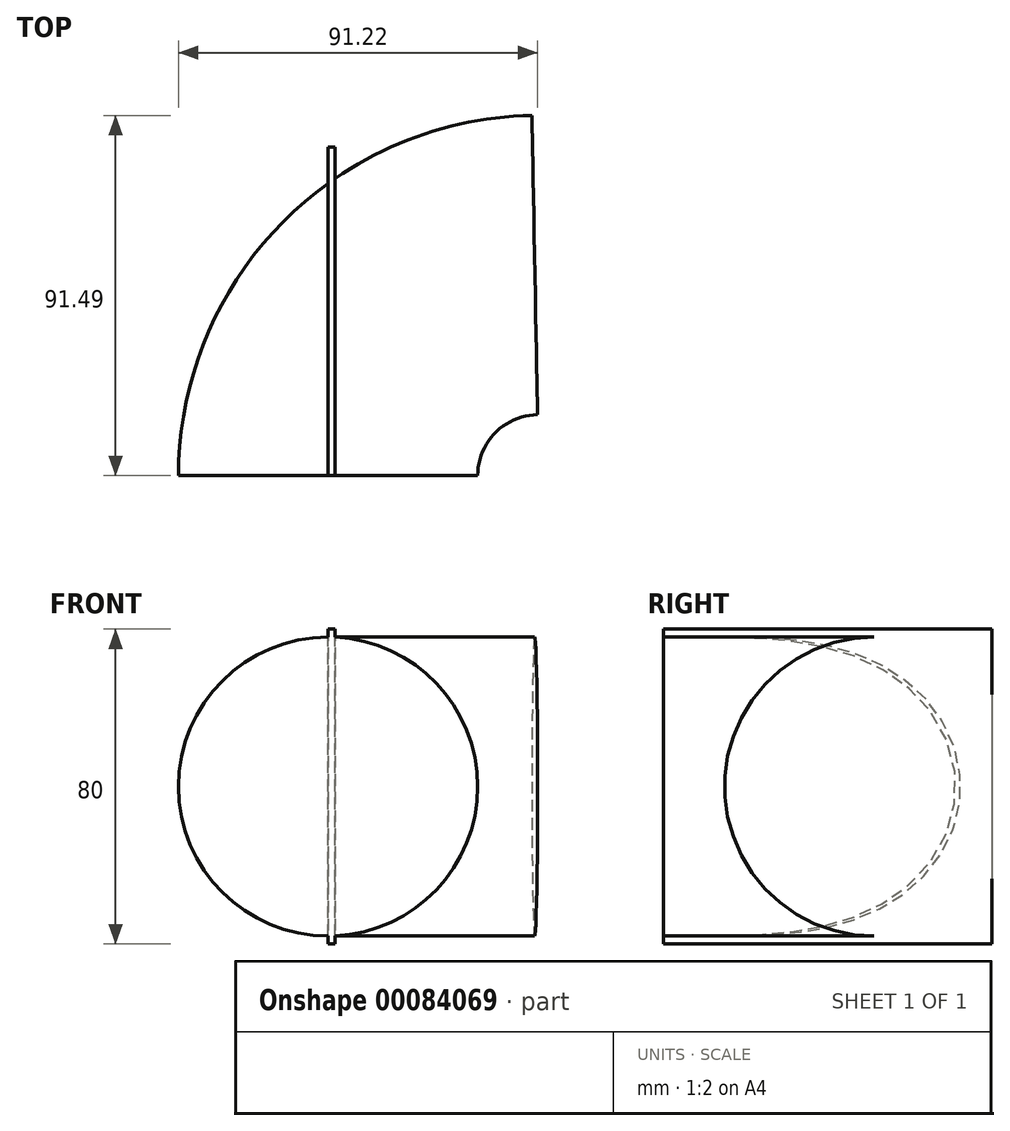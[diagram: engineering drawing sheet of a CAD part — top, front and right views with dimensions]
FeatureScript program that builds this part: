
annotation { "Feature Type Name" : "Feature", "Feature Type Description" : "" }
export const myFeature = defineFeature(function(context is Context, id is Id, definition is map)
    precondition{}
    {
        {
            var Q0;
            Q0=qCreatedBy(makeId("Front.planeOp"),FACE);
            var sketch = newSketch(context, id + "F0", { "sketchPlane" : qUnion([Q0])});
            skCircle(sketch, "E0", {"center": v(0, 0) * mm, "radius": 38 * mm});
            skSolve(sketch);
        }
        {
            var Q0;
            Q0=qCreatedBy(makeId("Top.planeOp"),FACE);
            var sketch = newSketch(context, id + "F1", { "sketchPlane" : qUnion([Q0])});
            skArc(sketch, "E1", {"start": v(0, 0) * mm, "mid": v(15.32, 37.48) * mm, "end": v(52.5, 53.5) * mm});
            skSolve(sketch);
        }
        {
            var Q0;
            Q0=makeQuery(id+"F0.imprint","IMPRINT",FACE,{"disambiguationData":[TD([[makeQuery(id+"F0.imprint","IMPRINT",EDGE,{"derivedFrom":sQuery(id+"F0.wireOp",EDGE,"E0")}),1.0]])]});
            var Q1;
            Q1=sQuery(id+"F1.wireOp",EDGE,"E1");
            sweep(context, id + "F2", {"profiles" : qUnion([Q0]), "path" : qUnion([Q1])});
        }
        {
            var Q0;
            Q0=qCreatedBy(makeId("Top.planeOp"),FACE);
            var sketch = newSketch(context, id + "F3", { "sketchPlane" : qUnion([Q0])});
            skLineSegment(sketch, "E2.bottom", {"start": v(0, 0) * mm, "end": v(1.78, 0) * mm});
            skLineSegment(sketch, "E2.top", {"start": v(0, 83.4) * mm, "end": v(1.78, 83.4) * mm});
            skLineSegment(sketch, "E2.left", {"start": v(0, 0) * mm, "end": v(0, 83.4) * mm});
            skLineSegment(sketch, "E2.right", {"start": v(1.78, 0) * mm, "end": v(1.78, 83.4) * mm});
            skSolve(sketch);
        }
        {
            var Q0;
            Q0=makeQuery(id+"F3.imprint","IMPRINT",FACE,{"disambiguationData":[TD([[makeQuery(id+"F3.imprint","IMPRINT",EDGE,{"derivedFrom":sQuery(id+"F3.wireOp",EDGE,"E2.bottom")}),1.0]])]});
            extrude(context, id + "F4", {"entities" : qUnion([Q0]), "operationType" : NewBodyOperationType.ADD, "endBound" : BoundingType.SYMMETRIC, "depth" : 80 * mm});
        }
    });
